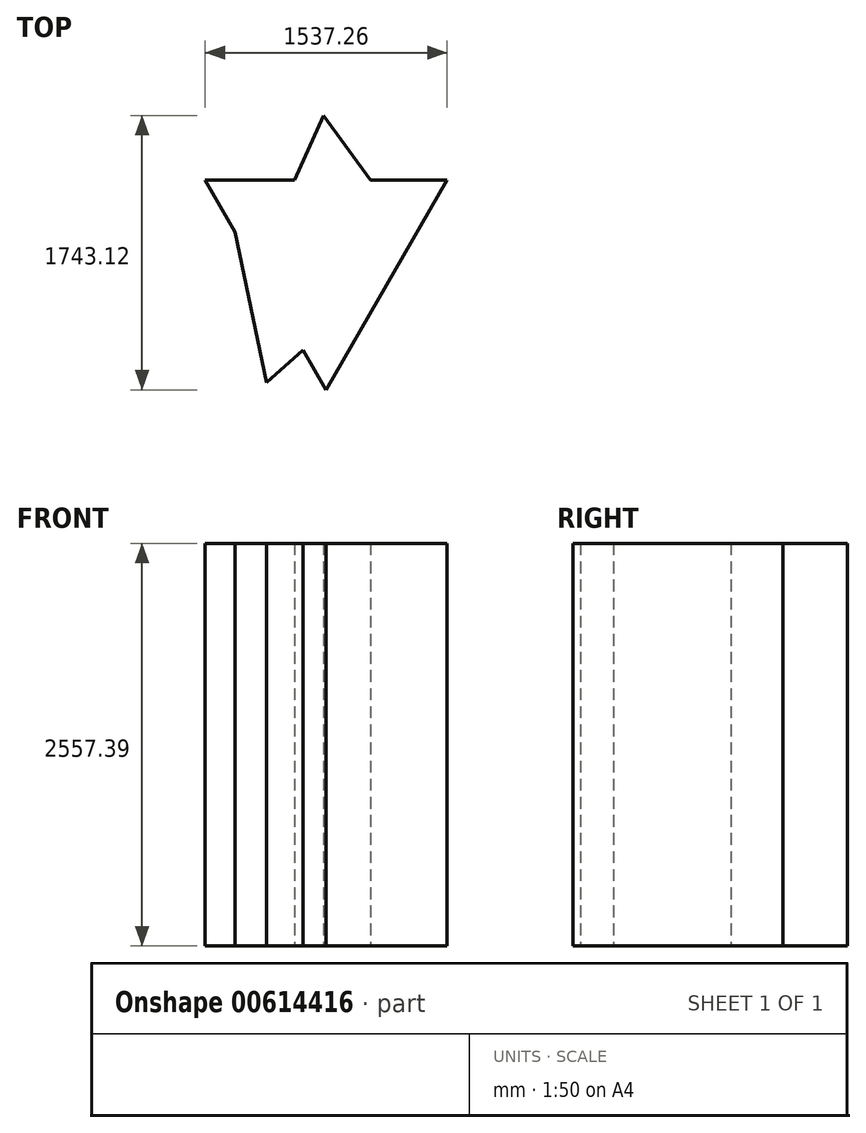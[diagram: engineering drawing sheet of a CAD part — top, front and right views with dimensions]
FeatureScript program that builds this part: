
annotation { "Feature Type Name" : "Feature", "Feature Type Description" : "" }
export const myFeature = defineFeature(function(context is Context, id is Id, definition is map)
    precondition{}
    {
        {
            var Q0;
            Q0=qCreatedBy(makeId("Top.planeOp"),FACE);
            var sketch = newSketch(context, id + "F0", { "sketchPlane" : qUnion([Q0])});
            skCircle(sketch, "E0.cCircle", {"center": v(-308.05, -252.25) * mm, "radius": 443.77 * mm, "construction": true});
            skLineSegment(sketch, "E0.0", {"start": v(-1076.68, 191.52) * mm, "end": v(460.58, 191.52) * mm});
            skLineSegment(sketch, "E0.1", {"start": v(460.58, 191.52) * mm, "end": v(-308.05, -1139.79) * mm});
            skLineSegment(sketch, "E0.2", {"start": v(-308.05, -1139.79) * mm, "end": v(-1076.68, 191.52) * mm});
            skPoint(sketch, "E0.0.midPoint", {"position": v(-308.05, 191.52) * mm});
            skCircle(sketch, "E1.cCircle", {"center": v(-508.58, -548.63) * mm, "radius": 286.07 * mm, "construction": true});
            skLineSegment(sketch, "E1.0", {"start": v(-890.5, -122.62) * mm, "end": v(51.32, -430.9) * mm});
            skLineSegment(sketch, "E1.1", {"start": v(51.32, -430.9) * mm, "end": v(-686.56, -1092.39) * mm});
            skLineSegment(sketch, "E1.2", {"start": v(-686.56, -1092.39) * mm, "end": v(-890.5, -122.62) * mm});
            skPoint(sketch, "E1.0.midPoint", {"position": v(-419.59, -276.75) * mm});
            skCircle(sketch, "E2.cCircle", {"center": v(-262.38, 0) * mm, "radius": 303.32 * mm, "construction": true});
            skLineSegment(sketch, "E2.0", {"start": v(-753.2, -356.53) * mm, "end": v(-325.72, 603.33) * mm});
            skLineSegment(sketch, "E2.1", {"start": v(-325.72, 603.33) * mm, "end": v(291.8, -246.8) * mm});
            skLineSegment(sketch, "E2.2", {"start": v(291.8, -246.8) * mm, "end": v(-753.2, -356.53) * mm});
            skPoint(sketch, "E2.0.midPoint", {"position": v(-539.46, 123.4) * mm});
            skSolve(sketch);
        }
        {
            var Q0;
            {var subQ5=sQuery(id+"F0.wireOp",EDGE,"E0.2");var subQ6=sQuery(id+"F0.wireOp",EDGE,"E0.0");var subQ7=makeQuery(id+"F0.imprint","INTERSECT",VERTEX,{"derivedFrom":[subQ6,subQ5]});Q0=makeQuery(id+"F0.imprint","IMPRINT",FACE,{"disambiguationData":[TD([[makeQuery(id+"F0.imprint","IMPRINT",EDGE,{"disambiguationData":[TD([[subQ7,-1.0]])],"derivedFrom":subQ6}),-1.0]])]});}
            var Q1;
            {var subQ3=sQuery(id+"F0.wireOp",EDGE,"E0.2");var subQ6=sQuery(id+"F0.wireOp",EDGE,"E0.1");var subQ9=makeQuery(id+"F0.imprint","INTERSECT",VERTEX,{"derivedFrom":[subQ6,subQ3]});Q1=makeQuery(id+"F0.imprint","IMPRINT",FACE,{"disambiguationData":[TD([[makeQuery(id+"F0.imprint","IMPRINT",EDGE,{"disambiguationData":[TD([[subQ9,1.0]])],"derivedFrom":subQ6}),-1.0]])]});}
            var Q2;
            {var subQ0=sQuery(id+"F0.wireOp",EDGE,"E1.1");var subQ1=sQuery(id+"F0.wireOp",EDGE,"E0.2");var subQ2=makeQuery(id+"F0.imprint","INTERSECT",VERTEX,{"derivedFrom":[subQ1,subQ0]});Q2=makeQuery(id+"F0.imprint","IMPRINT",FACE,{"disambiguationData":[TD([[makeQuery(id+"F0.imprint","IMPRINT",EDGE,{"disambiguationData":[TD([[subQ2,-1.0]])],"derivedFrom":subQ1}),1.0]])]});}
            var Q3;
            {var subQ0=sQuery(id+"F0.wireOp",EDGE,"E1.1");var subQ9=sQuery(id+"F0.wireOp",EDGE,"E0.2");var subQ10=makeQuery(id+"F0.imprint","INTERSECT",VERTEX,{"derivedFrom":[subQ9,subQ0]});Q3=makeQuery(id+"F0.imprint","IMPRINT",FACE,{"disambiguationData":[TD([[makeQuery(id+"F0.imprint","IMPRINT",EDGE,{"disambiguationData":[TD([[subQ10,-1.0]])],"derivedFrom":subQ9}),-1.0]])]});}
            var Q4;
            {var subQ0=sQuery(id+"F0.wireOp",EDGE,"E2.0");var subQ1=sQuery(id+"F0.wireOp",EDGE,"E0.0");var subQ2=makeQuery(id+"F0.imprint","INTERSECT",VERTEX,{"derivedFrom":[subQ1,subQ0]});Q4=makeQuery(id+"F0.imprint","IMPRINT",FACE,{"disambiguationData":[TD([[makeQuery(id+"F0.imprint","IMPRINT",EDGE,{"disambiguationData":[TD([[subQ2,-1.0]])],"derivedFrom":subQ1}),-1.0]])]});}
            var Q5;
            {var subQ0=sQuery(id+"F0.wireOp",EDGE,"E2.0");var subQ1=sQuery(id+"F0.wireOp",EDGE,"E0.0");var subQ2=makeQuery(id+"F0.imprint","INTERSECT",VERTEX,{"derivedFrom":[subQ1,subQ0]});Q5=makeQuery(id+"F0.imprint","IMPRINT",FACE,{"disambiguationData":[TD([[makeQuery(id+"F0.imprint","IMPRINT",EDGE,{"disambiguationData":[TD([[subQ2,-1.0]])],"derivedFrom":subQ1}),1.0]])]});}
            var Q6;
            {var subQ0=sQuery(id+"F0.wireOp",EDGE,"E0.1");var subQ1=sQuery(id+"F0.wireOp",EDGE,"E0.0");var subQ2=makeQuery(id+"F0.imprint","INTERSECT",VERTEX,{"derivedFrom":[subQ1,subQ0]});Q6=makeQuery(id+"F0.imprint","IMPRINT",FACE,{"disambiguationData":[TD([[makeQuery(id+"F0.imprint","IMPRINT",EDGE,{"disambiguationData":[TD([[subQ2,1.0]])],"derivedFrom":subQ1}),-1.0]])]});}
            var Q7;
            {var subQ0=sQuery(id+"F0.wireOp",EDGE,"E2.0");var subQ1=sQuery(id+"F0.wireOp",EDGE,"E1.0");var subQ2=makeQuery(id+"F0.imprint","INTERSECT",VERTEX,{"derivedFrom":[subQ1,subQ0]});Q7=makeQuery(id+"F0.imprint","IMPRINT",FACE,{"disambiguationData":[TD([[makeQuery(id+"F0.imprint","IMPRINT",EDGE,{"disambiguationData":[TD([[subQ2,-1.0]])],"derivedFrom":subQ1}),-1.0]])]});}
            extrude(context, id + "F1", {"entities" : qUnion([Q0, Q1, Q2, Q3, Q4, Q5, Q6, Q7]), "depth" : 2557.4 * mm, "offsetDistance" : 25.4 * mm});
        }
    });
